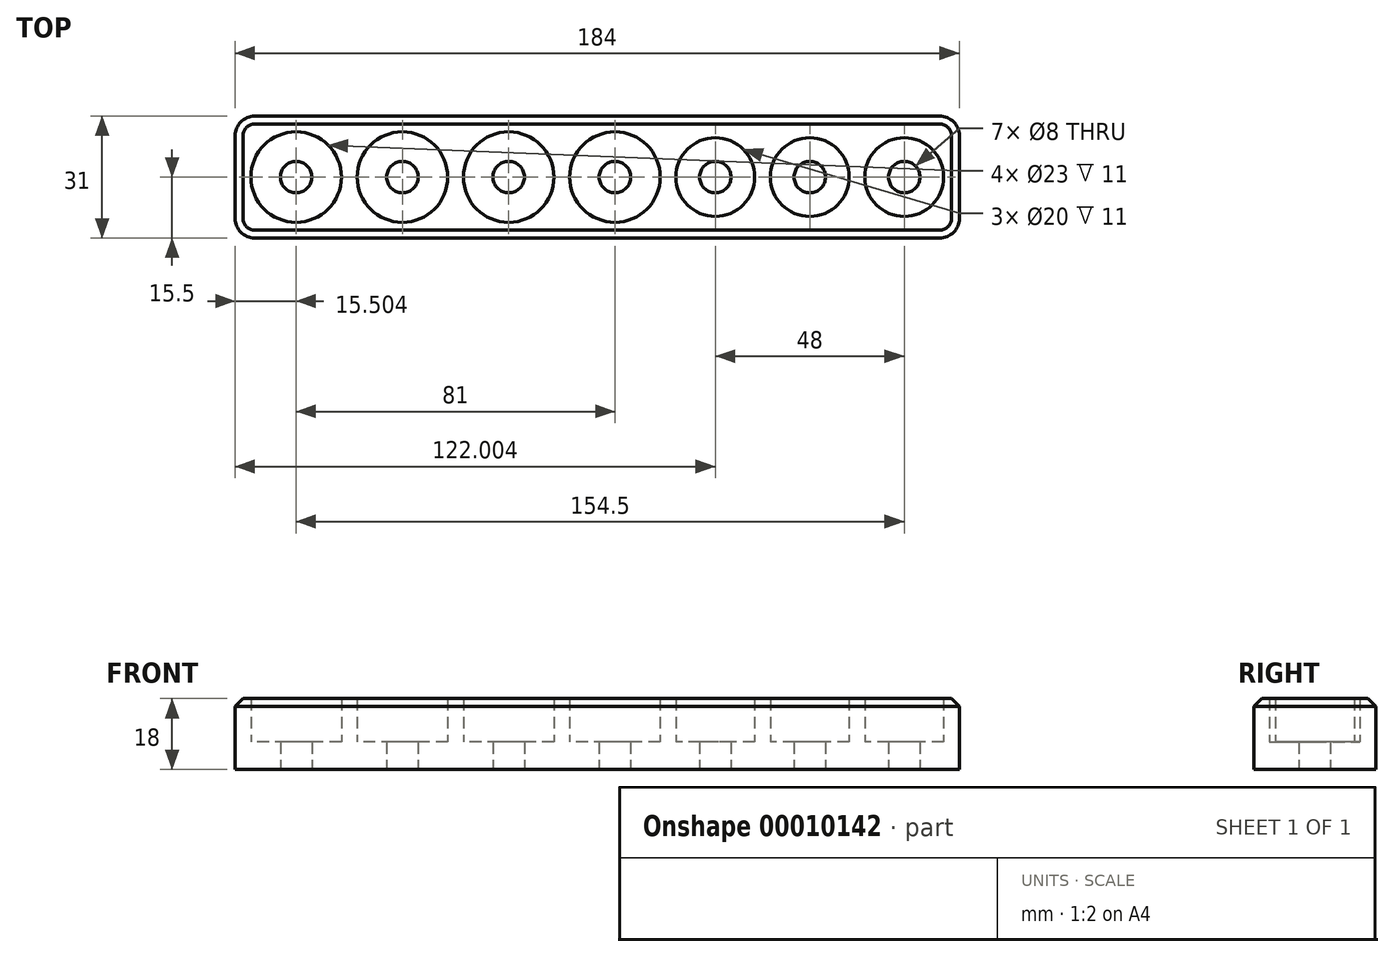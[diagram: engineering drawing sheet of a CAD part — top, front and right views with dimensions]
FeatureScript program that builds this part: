
annotation { "Feature Type Name" : "Feature", "Feature Type Description" : "" }
export const myFeature = defineFeature(function(context is Context, id is Id, definition is map)
    precondition{}
    {
        {
            var Q0;
            Q0=qCreatedBy(makeId("Top.planeOp"),FACE);
            var sketch = newSketch(context, id + "F0", { "sketchPlane" : qUnion([Q0])});
            skLineSegment(sketch, "E0.bottom", {"start": v(-64.07, 15.5) * mm, "end": v(119.93, 15.5) * mm});
            skLineSegment(sketch, "E0.top", {"start": v(-64.07, -15.5) * mm, "end": v(119.93, -15.5) * mm});
            skLineSegment(sketch, "E0.left", {"start": v(-64.07, 15.5) * mm, "end": v(-64.07, -15.5) * mm});
            skLineSegment(sketch, "E0.right", {"start": v(119.93, 15.5) * mm, "end": v(119.93, -15.5) * mm});
            skCircle(sketch, "E1", {"center": v(-48.57, 0) * mm, "radius": 11.5 * mm});
            skPoint(sketch, "E2", {"position": v(-64.07, 0) * mm});
            skCircle(sketch, "E3.1.0.0", {"center": v(-21.57, 0) * mm, "radius": 11.5 * mm});
            skCircle(sketch, "E3.2.0.0", {"center": v(5.43, 0) * mm, "radius": 11.5 * mm});
            skCircle(sketch, "E3.3.0.0", {"center": v(32.43, 0) * mm, "radius": 11.5 * mm});
            skLineSegment(sketch, "E3.direction1", {"start": v(-48.57, 0) * mm, "end": v(-21.57, 0) * mm, "construction": true});
            skCircle(sketch, "E4", {"center": v(-48.57, 0) * mm, "radius": 4 * mm});
            skCircle(sketch, "E5.1.0.0", {"center": v(-21.57, 0) * mm, "radius": 4 * mm});
            skCircle(sketch, "E5.2.0.0", {"center": v(5.43, 0) * mm, "radius": 4 * mm});
            skCircle(sketch, "E5.3.0.0", {"center": v(32.43, 0) * mm, "radius": 4 * mm});
            skCircle(sketch, "E6", {"center": v(57.93, 0) * mm, "radius": 10 * mm});
            skCircle(sketch, "E7", {"center": v(57.93, 0) * mm, "radius": 4 * mm});
            skCircle(sketch, "E8.1.0.0", {"center": v(81.93, 0) * mm, "radius": 4 * mm});
            skCircle(sketch, "E8.1.0.1", {"center": v(81.93, 0) * mm, "radius": 10 * mm});
            skCircle(sketch, "E8.2.0.0", {"center": v(105.93, 0) * mm, "radius": 4 * mm});
            skCircle(sketch, "E8.2.0.1", {"center": v(105.93, 0) * mm, "radius": 10 * mm});
            skLineSegment(sketch, "E8.direction1", {"start": v(57.93, 0) * mm, "end": v(81.93, 0) * mm, "construction": true});
            skSolve(sketch);
        }
        {
            var Q0;
            Q0=makeQuery(id+"F0.imprint","IMPRINT",FACE,{"disambiguationData":[TD([[makeQuery(id+"F0.imprint","IMPRINT",EDGE,{"derivedFrom":sQuery(id+"F0.wireOp",EDGE,"E0.bottom")}),-1.0]])]});
            var Q1;
            Q1=makeQuery(id+"F0.imprint","IMPRINT",FACE,{"disambiguationData":[TD([[makeQuery(id+"F0.imprint","IMPRINT",EDGE,{"derivedFrom":sQuery(id+"F0.wireOp",EDGE,"E1")}),1.0]])]});
            var Q2;
            Q2=makeQuery(id+"F0.imprint","IMPRINT",FACE,{"disambiguationData":[TD([[makeQuery(id+"F0.imprint","IMPRINT",EDGE,{"derivedFrom":sQuery(id+"F0.wireOp",EDGE,"E3.1.0.0")}),1.0]])]});
            var Q3;
            Q3=makeQuery(id+"F0.imprint","IMPRINT",FACE,{"disambiguationData":[TD([[makeQuery(id+"F0.imprint","IMPRINT",EDGE,{"derivedFrom":sQuery(id+"F0.wireOp",EDGE,"E3.2.0.0")}),1.0]])]});
            var Q4;
            Q4=makeQuery(id+"F0.imprint","IMPRINT",FACE,{"disambiguationData":[TD([[makeQuery(id+"F0.imprint","IMPRINT",EDGE,{"derivedFrom":sQuery(id+"F0.wireOp",EDGE,"E3.3.0.0")}),1.0]])]});
            var Q5;
            Q5=makeQuery(id+"F0.imprint","IMPRINT",FACE,{"disambiguationData":[TD([[makeQuery(id+"F0.imprint","IMPRINT",EDGE,{"derivedFrom":sQuery(id+"F0.wireOp",EDGE,"E6")}),1.0]])]});
            var Q6;
            Q6=makeQuery(id+"F0.imprint","IMPRINT",FACE,{"disambiguationData":[TD([[makeQuery(id+"F0.imprint","IMPRINT",EDGE,{"derivedFrom":sQuery(id+"F0.wireOp",EDGE,"E8.1.0.0")}),-1.0]])]});
            var Q7;
            Q7=makeQuery(id+"F0.imprint","IMPRINT",FACE,{"disambiguationData":[TD([[makeQuery(id+"F0.imprint","IMPRINT",EDGE,{"derivedFrom":sQuery(id+"F0.wireOp",EDGE,"E8.2.0.0")}),-1.0]])]});
            extrude(context, id + "F1", {"entities" : qUnion([Q0, Q1, Q2, Q3, Q4, Q5, Q6, Q7]), "depth" : 7 * mm});
        }
        {
            var Q0;
            Q0 = qSketchRegion(id + "F0", true);
            extrude(context, id + "F2", {"entities" : qUnion([Q0]), "operationType" : NewBodyOperationType.ADD, "depth" : 18 * mm});
        }
        {
            var Q0;
            {var subQ0=sQuery(id+"F0.wireOp",EDGE,"E0.top");var subQ1=sQuery(id+"F0.wireOp",EDGE,"E0.left");Q0=makeQuery(id+"F2.boolean.opBoolean","MERGE",EDGE,{"derivedFrom":[makeQuery(id+"F1.opExtrude","SWEPT_EDGE",EDGE,{"disambiguationData":[OSD([subQ0,subQ1])]}),makeQuery(id+"F2.opExtrude","SWEPT_EDGE",EDGE,{"disambiguationData":[OSD([subQ0,subQ1])]})]});}
            var Q1;
            {var subQ0=sQuery(id+"F0.wireOp",EDGE,"E0.bottom");var subQ1=sQuery(id+"F0.wireOp",EDGE,"E0.left");Q1=makeQuery(id+"F2.boolean.opBoolean","MERGE",EDGE,{"derivedFrom":[makeQuery(id+"F1.opExtrude","SWEPT_EDGE",EDGE,{"disambiguationData":[OSD([subQ0,subQ1])]}),makeQuery(id+"F2.opExtrude","SWEPT_EDGE",EDGE,{"disambiguationData":[OSD([subQ0,subQ1])]})]});}
            var Q2;
            {var subQ0=sQuery(id+"F0.wireOp",EDGE,"E0.top");var subQ1=sQuery(id+"F0.wireOp",EDGE,"E0.right");Q2=makeQuery(id+"F2.boolean.opBoolean","MERGE",EDGE,{"derivedFrom":[makeQuery(id+"F1.opExtrude","SWEPT_EDGE",EDGE,{"disambiguationData":[OSD([subQ0,subQ1])]}),makeQuery(id+"F2.opExtrude","SWEPT_EDGE",EDGE,{"disambiguationData":[OSD([subQ0,subQ1])]})]});}
            var Q3;
            {var subQ0=sQuery(id+"F0.wireOp",EDGE,"E0.bottom");var subQ1=sQuery(id+"F0.wireOp",EDGE,"E0.right");Q3=makeQuery(id+"F2.boolean.opBoolean","MERGE",EDGE,{"derivedFrom":[makeQuery(id+"F1.opExtrude","SWEPT_EDGE",EDGE,{"disambiguationData":[OSD([subQ0,subQ1])]}),makeQuery(id+"F2.opExtrude","SWEPT_EDGE",EDGE,{"disambiguationData":[OSD([subQ0,subQ1])]})]});}
            fillet(context, id + "F3", {"entities" : qUnion([Q0, Q1, Q2, Q3]), "radius" : 5 * mm, "tangentPropagation" : true, "allowEdgeOverflow" : false});
        }
        {
            var Q0;
            Q0=makeQuery(id+"F2.opExtrude","CAP_EDGE",EDGE,{"disambiguationData":[OSD([sQuery(id+"F0.wireOp",EDGE,"E0.top")])],"isStart":false});
            chamfer(context, id + "F4", {"entities" : qUnion([Q0]), "width" : 2 * mm, "tangentPropagation" : true});
        }
    });
